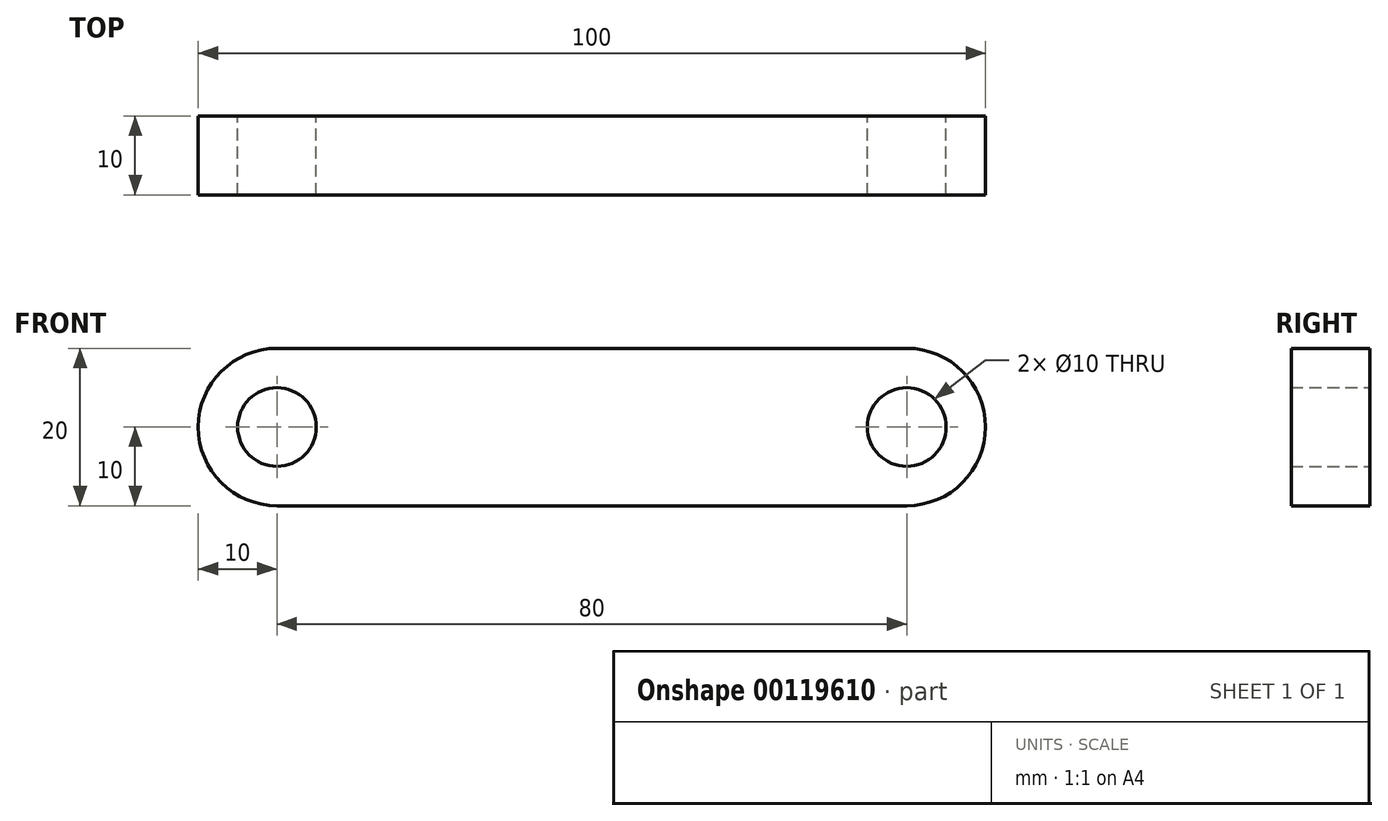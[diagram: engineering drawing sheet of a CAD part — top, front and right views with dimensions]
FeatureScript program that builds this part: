
annotation { "Feature Type Name" : "Feature", "Feature Type Description" : "" }
export const myFeature = defineFeature(function(context is Context, id is Id, definition is map)
    precondition{}
    {
        {
            var Q0;
            Q0=qCreatedBy(makeId("Front.planeOp"),FACE);
            var sketch = newSketch(context, id + "F0", { "sketchPlane" : qUnion([Q0])});
            skLineSegment(sketch, "E0", {"start": v(0, 20) * mm, "end": v(80, 20) * mm});
            skLineSegment(sketch, "E1", {"start": v(0, 0) * mm, "end": v(80, 0) * mm});
            skArc(sketch, "E2", {"start": v(0, 20) * mm, "mid": v(-10, 10) * mm, "end": v(0, 0) * mm});
            skArc(sketch, "E3", {"start": v(80, 0) * mm, "mid": v(90, 10) * mm, "end": v(80, 20) * mm});
            skCircle(sketch, "E4", {"center": v(0, 10) * mm, "radius": 5 * mm});
            skCircle(sketch, "E5", {"center": v(80, 10) * mm, "radius": 5 * mm});
            skSolve(sketch);
        }
        {
            var Q0;
            Q0 = qSketchRegion(id + "F0", true);
            extrude(context, id + "F1", {"entities" : qUnion([Q0]), "depth" : 10 * mm});
        }
    });
